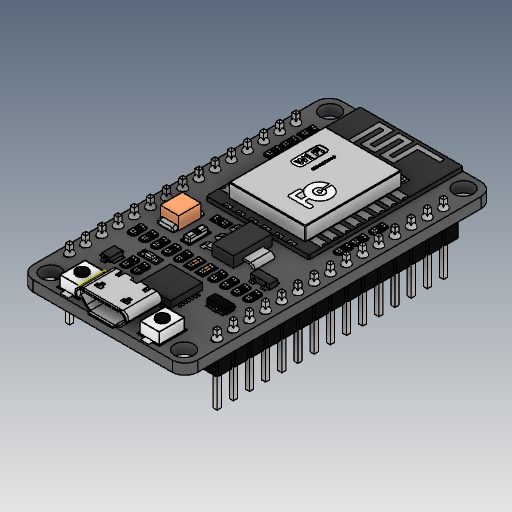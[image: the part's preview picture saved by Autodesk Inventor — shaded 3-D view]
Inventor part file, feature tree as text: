
AUTODESK INVENTOR PART (.ipt)
format: ipt  version: 2020.1 (Build 241239000, 239)  size: 9,712,640 bytes
history: native  units: mm
features: other x70, move_body x22, mirror x6, plane x3, boolean_combine x3, extrude x3, pattern_linear x3, sketch x2, projected_geometry x1
ambient origin geometry x8: Origin, YZ Plane, XZ Plane, XY Plane, X Axis, Y Axis, Z Axis, Center Point
bodies: Solid18 (feature_tree), Solid19 (feature_tree)
feature tree (113):
  other  "Glass board for 8266.ipt"
  other  "MicroUSB_Socket.ipt"
  other  "MicroButton.ipt"
  other  "WiFi Board.ipt"
  other  "SmallRectangleChip.ipt"
  other  "SmallMicroChip2.ipt"
  other  "SmallMicroChip.ipt"
  other  "Transistor_2-leg.ipt"
  other  "Transistor_3-leg.ipt"
  other  "LED Diode.ipt"
  other  "Contact Pin Set - 15.ipt"
  other  "MicroResistor.ipt"
  other  "MicroResistor-LittleLarger.ipt"
  move_body  "Move Body1"
  move_body  "Move Body2"
  move_body  "Move Body3"
  move_body  "Move Body4"
  plane  "Work Plane1"
  mirror  "Mirror1"
  boolean_combine  "Combine1"
  move_body  "Move Body5"
  move_body  "Move Body6"
  move_body  "Move Body7"
  move_body  "Move Body8"
  move_body  "Move Body9"
  move_body  "Move Body10"
  move_body  "Move Body11"
  move_body  "Move Body12"
  move_body  "Move Body13"
  move_body  "Move Body14"
  mirror  "Mirror2"
  extrude  "Extrusion1"  Depth=10.0mm
  pattern_linear  "Rectangular Pattern1"  Spacing1=4.0mm  [1 undecoded]
  boolean_combine  "Combine2"
  extrude  "Extrusion2"  Depth=0.5mm
  pattern_linear  "Rectangular Pattern2"  Spacing1=10.0mm  [1 undecoded]
  move_body  "Move Body15"
  move_body  "Move Body16"
  pattern_linear  "Rectangular Pattern3"  Spacing1=1.65mm  [1 undecoded]
  move_body  "Move Body17"
  plane  "Work Plane2"
  mirror  "Mirror3"
  move_body  "Move Body18"
  plane  "Work Plane3"
  mirror  "Mirror4"
  move_body  "Move Body19"
  mirror  "Mirror5"
  move_body  "Move Body20"
  boolean_combine  "Combine3"
  mirror  "Mirror6"
  move_body  "Move Body21"
  move_body  "Move Body22"
  extrude  "Extrusion3"  Depth=0.5mm
  other  "Solid1::Glass board for 8266.ipt"
  other  "TaggingFeature1"
  other  "Solid1::MicroUSB_Socket.ipt"
  other  "TaggingFeature2"
  other  "Solid1::MicroButton.ipt"
  other  "TaggingFeature3"
  other  "Solid1::WiFi Board.ipt"
  other  "Solid2::WiFi Board.ipt"
  other  "TaggingFeature4"
  other  "Solid1::SmallRectangleChip.ipt"
  other  "TaggingFeature5"
  other  "Solid1::SmallMicroChip2.ipt"
  other  "TaggingFeature6"
  other  "Solid1::SmallMicroChip.ipt"
  other  "TaggingFeature7"
  other  "Solid3::Transistor_2-leg.ipt"
  other  "TaggingFeature8"
  other  "Solid1::Transistor_3-leg.ipt"
  other  "TaggingFeature9"
  other  "Solid1::Transistor_3-leg.ipt_1"
  other  "TaggingFeature10"
  other  "Solid1::LED Diode.ipt"
  other  "TaggingFeature11"
  other  "Solid1::Contact Pin Set - 15.ipt"
  other  "TaggingFeature12"
  sketch  "Sketch1"  dims[d0=10.0mm d1=10.0mm]
  projected_geometry  "Projected Loop1"
  sketch  "Sketch2"  dims[d2=90.0deg d3=4.0mm d4=21.5mm d5=3.25mm d6=0.5mm d7=10.0mm d8=1.65mm d9=23.0mm d10=4.75mm d11=10.0mm d12=1.655mm d13=12.075mm d14=10.0mm d15=90.0deg d16=1.651mm d17=10.25mm d18=2.75mm d19=10.0mm d20=90.0deg d21=1.652mm d22=9.0mm d23=9.0mm d24=10.0mm d25=1.652mm d26=14.75mm d27=1.25mm d28=10.0mm d29=1.651mm d30=15.75mm d31=8.5mm d32=10.0mm d33=1.652mm d34=8.75mm d35=9.0mm d36=90.0deg d37=10.0mm d38=1.652mm d39=90.0deg d40=9.5mm d41=1.35mm d42=10.0mm d43=1.651mm d44=10.0mm d45=90.0deg d46=1.25mm d47=10.0mm d48=90.0deg d49=9.75mm d50=0.85mm d51=7.9mm d52=1.0mm d53=6.515mm d54=10.0mm d55=0.0mm d56=150.0mm d58=2.54mm d59=20.0mm d61=23.0mm d62=0.8mm d63=-4.363323mm d64=1.31mm d65=150.0mm d67=2.52mm d68=20.0mm d70=23.0mm d71=10.0mm d72=1.651mm d73=5.0mm d74=2.0mm d75=10.0mm d76=1.651mm d77=90.0deg d78=9.5mm d79=8.0mm d80=110.0mm d82=1.8mm d83=10.0mm d84=1.651mm d85=10.0mm d86=90.0deg d87=4.25mm d88=0.0mm d89=10.0mm d90=1.651mm d91=10.0mm d92=90.0deg d93=2.75mm d94=10.0mm d95=10.0mm d96=0.0mm d97=1.0mm d98=1.5mm d99=7.75mm d100=10.0mm d101=1.651mm d102=90.0deg d103=6.25mm d104=2.5mm d105=1.1mm d107=2.25mm d108=0.08mm d109=0.15mm d110=1.1mm d111=2.25mm d112=1.1mm d113=2.25mm d114=0.15mm d115=0.4mm d116=0.15mm d117=1.1mm d118=2.25mm d119=0.4mm d120=1.1mm d121=2.25mm d122=0.4mm d123=1.1mm d124=2.25mm d125=0.4mm d126=1.1mm d127=2.25mm d128=0.4mm d129=1.1mm d130=2.25mm d131=0.4mm d132=1.1mm d133=2.25mm d134=0.4mm d135=1.1mm d136=2.25mm d137=0.4mm d138=1.1mm d139=2.25mm d140=0.4mm d141=1.1mm d142=2.25mm d143=0.4mm d144=1.1mm d145=2.25mm d146=0.4mm d147=1.1mm d148=2.25mm d149=0.4mm d150=1.1mm d151=2.25mm d152=0.4mm d153=1.1mm d154=2.25mm d155=0.4mm d156=1.1mm d157=2.25mm d158=0.4mm d159=1.1mm d160=2.25mm d161=0.4mm d162=1.1mm d163=2.25mm d165=0.1mm d166=0.1mm d167=0.1mm d168=0.1mm d169=0.1mm d170=0.1mm d171=0.1mm d172=0.1mm d173=0.1mm d174=0.1mm d175=0.1mm d176=0.1mm d177=0.1mm d178=0.1mm d179=0.1mm d180=0.1mm d181=0.1mm d182=0.1mm d183=0.1mm d184=0.1mm d185=1.3mm d186=3.3mm d187=0.1mm d188=0.1mm d189=0.1mm d190=0.1mm d191=0.1mm d192=0.1mm d193=1.1mm d194=2.25mm d195=0.1mm d196=0.1mm d197=0.1mm d198=0.1mm d199=0.1mm d200=0.1mm d201=1.1mm d202=2.75mm d203=0.1mm d204=0.1mm d205=0.1mm d206=0.1mm d207=0.1mm d208=0.1mm d210=0.15mm d211=0.15mm d212=0.1mm d213=0.4mm d215=0.1mm d216=0.1mm d217=0.1mm d218=0.1mm d219=2.5mm d220=2.5mm d221=0.4mm d222=0.15mm d223=0.15mm d224=0.15mm d225=0.15mm d226=0.2mm d227=0.2mm d228=0.1mm d229=0.1mm d230=0.1mm d231=0.1mm d232=0.1mm d233=0.1mm d235=0.15mm d236=0.15mm d237=0.15mm d238=0.15mm d239=0.5mm d240=0.5mm d241=0.15mm d242=0.1mm d243=0.15mm d244=0.15mm d245=0.15mm d246=0.1mm d247=0.1mm d248=0.1mm d249=0.15mm d250=0.15mm d251=0.1mm d252=0.1mm d253=0.1mm d254=0.1mm d255=0.15mm d256=0.15mm d257=0.1mm d258=0.1mm d259=0.15mm d260=0.15mm d261=0.1mm d262=0.1mm d263=0.001mm d264=0.0mm]
  other  "Solid1::MicroResistor.ipt"
  other  "TaggingFeature13"
  other  "Solid1::MicroResistor.ipt_1"
  other  "TaggingFeature14"
  other  "Solid1::MicroResistor.ipt_2"
  other  "TaggingFeature15"
  other  "Solid1::MicroResistor.ipt_3"
  other  "TaggingFeature16"
  other  "Pattern of Resistor4:1"
  other  "Pattern of Resistor4:2"
  other  "Pattern of Resistor4:3"
  other  "Resistor5"
  other  "Solid1::MicroResistor-LittleLarger.ipt"
  other  "TaggingFeature17"
  other  "MainBoard"
  other  "USB_Socket"
  other  "ButtonFlash"
  other  "WiFi_Board"
  other  "WiFi_Card"
  other  "RectangularChip"
  other  "TanChip"
  other  "MicroChip"
  other  "Transistor_2-leg"
  other  "Transistor_3-leg"
  other  "Transistor_3-leg2"
  other  "LED_Diode 1"
  other  "ContactPins"
  other  "Resistor1"
  other  "Resistor2"
  other  "Resistor3"
  other  "Resistor4"
  other  "LargeResistor"
note: 3 required parameter values undecoded (feature->parameter linkage not recoverable at this tier; creation-order binding heuristic only, values carry confidence <= 0.55)
